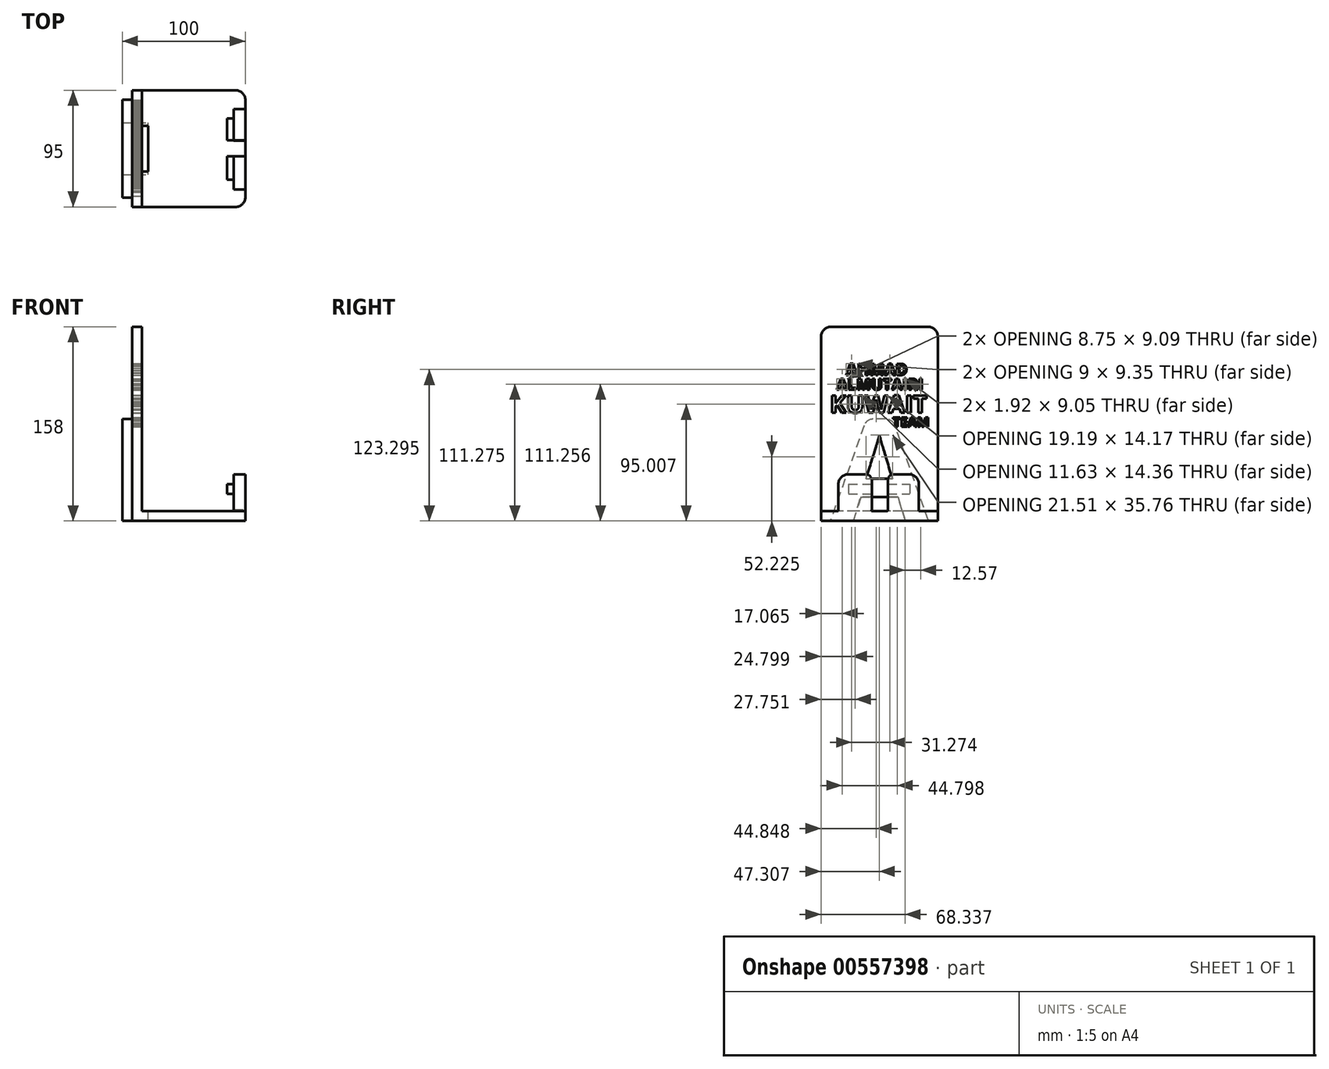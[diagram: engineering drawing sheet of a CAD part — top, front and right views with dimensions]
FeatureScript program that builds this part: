
annotation { "Feature Type Name" : "Feature", "Feature Type Description" : "" }
export const myFeature = defineFeature(function(context is Context, id is Id, definition is map)
    precondition{}
    {
        {
            var Q0;
            Q0=qCreatedBy(makeId("Top.planeOp"),FACE);
            var sketch = newSketch(context, id + "F0", { "sketchPlane" : qUnion([Q0])});
            skLineSegment(sketch, "E0.bottom", {"start": v(-46, -47.5) * mm, "end": v(46, -47.5) * mm});
            skLineSegment(sketch, "E0.top", {"start": v(-46, 47.5) * mm, "end": v(46, 47.5) * mm});
            skLineSegment(sketch, "E0.left", {"start": v(-46, -47.5) * mm, "end": v(-46, 47.5) * mm});
            skLineSegment(sketch, "E0.right", {"start": v(46, -47.5) * mm, "end": v(46, 47.5) * mm});
            skPoint(sketch, "E0.middle", {"position": v(0, 0) * mm});
            skSolve(sketch);
        }
        {
            var Q0;
            Q0=makeQuery(id+"F0.imprint","IMPRINT",FACE,{"disambiguationData":[TD([[makeQuery(id+"F0.imprint","IMPRINT",EDGE,{"derivedFrom":sQuery(id+"F0.wireOp",EDGE,"E0.bottom")}),1.0]])]});
            extrude(context, id + "F1", {"entities" : qUnion([Q0]), "depth" : 8 * mm, "offsetDistance" : 25 * mm});
        }
        {
            var Q0;
            Q0=makeQuery(id+"F1.opExtrude","CAP_FACE",FACE,{"disambiguationData":[OSD([sQuery(id+"F0.wireOp",EDGE,"E0.bottom"),sQuery(id+"F0.wireOp",EDGE,"E0.top"),sQuery(id+"F0.wireOp",EDGE,"E0.left"),sQuery(id+"F0.wireOp",EDGE,"E0.right")])],"isStart":false});
            var sketch = newSketch(context, id + "F2", { "sketchPlane" : qUnion([Q0])});
            skLineSegment(sketch, "E1.bottom", {"start": v(-46, 47.5) * mm, "end": v(-38, 47.5) * mm});
            skLineSegment(sketch, "E1.top", {"start": v(-46, -47.5) * mm, "end": v(-38, -47.5) * mm});
            skLineSegment(sketch, "E1.left", {"start": v(-46, 47.5) * mm, "end": v(-46, -47.5) * mm});
            skLineSegment(sketch, "E1.right", {"start": v(-38, 47.5) * mm, "end": v(-38, -47.5) * mm});
            skSolve(sketch);
        }
        {
            var Q0;
            Q0=qSketchRegion(id+"F2",true);
            extrude(context, id + "F3", {"entities" : qUnion([Q0]), "operationType" : NewBodyOperationType.ADD, "depth" : 150 * mm, "offsetDistance" : 25 * mm});
        }
        {
            var Q0;
            Q0=makeQuery(id+"F1.opExtrude","CAP_FACE",FACE,{"disambiguationData":[OSD([sQuery(id+"F0.wireOp",EDGE,"E0.bottom"),sQuery(id+"F0.wireOp",EDGE,"E0.top"),sQuery(id+"F0.wireOp",EDGE,"E0.left"),sQuery(id+"F0.wireOp",EDGE,"E0.right")])],"isStart":false});
            var sketch = newSketch(context, id + "F4", { "sketchPlane" : qUnion([Q0])});
            skLineSegment(sketch, "E2.bottom", {"start": v(46, 32.06) * mm, "end": v(36.5, 32.06) * mm});
            skLineSegment(sketch, "E2.top", {"start": v(46, -33.37) * mm, "end": v(36.5, -33.37) * mm});
            skLineSegment(sketch, "E2.left", {"start": v(46, 32.06) * mm, "end": v(46, -33.37) * mm});
            skLineSegment(sketch, "E2.right", {"start": v(36.5, 32.06) * mm, "end": v(36.5, -33.37) * mm});
            skSolve(sketch);
        }
        {
            var Q0;
            Q0=makeQuery(id+"F4.imprint","IMPRINT",FACE,{"disambiguationData":[TD([[makeQuery(id+"F4.imprint","IMPRINT",EDGE,{"derivedFrom":sQuery(id+"F4.wireOp",EDGE,"E2.bottom")}),1.0]])]});
            extrude(context, id + "F5", {"entities" : qUnion([Q0]), "operationType" : NewBodyOperationType.ADD, "depth" : 30 * mm, "offsetDistance" : 25 * mm});
        }
        {
            var Q0;
            Q0=makeQuery(id+"F3.boolean.opBoolean","MERGE",FACE,{"derivedFrom":[makeQuery(id+"F1.opExtrude","SWEPT_FACE",FACE,{"disambiguationData":[OSD([sQuery(id+"F0.wireOp",EDGE,"E0.left")])]}),makeQuery(id+"F3.opExtrude","SWEPT_FACE",FACE,{"disambiguationData":[OSD([sQuery(id+"F2.wireOp",EDGE,"E1.left")])]})]});
            var sketch = newSketch(context, id + "F6", { "sketchPlane" : qUnion([Q0])});
            skText(sketch, "E3", { "text": "A", "fontName": "OpenSans-Bold.ttf"});
            const initialGuessF6  = {"E3": [-0.03983, 0, 1, 0, 0.0833]};
            skSetInitialGuess(sketch, initialGuessF6);
            skSolve(sketch);
        }
        {
            var Q0;
            Q0=qSketchRegion(id+"F6",true);
            extrude(context, id + "F7", {"entities" : qUnion([Q0]), "operationType" : NewBodyOperationType.ADD, "depth" : 8 * mm, "offsetDistance" : 25 * mm});
        }
        {
            var Q0;
            Q0=makeQuery(id+"F7.boolean.opBoolean","SPLIT",FACE,{"disambiguationData":[TD([makeQuery(id+"F7.opExtrude","SWEPT_FACE",FACE,{"disambiguationData":[OSD([sQuery(id+"F6.wireOp",EDGE,"E3.sketch_text.stroke-8")])]})])],"derivedFrom":makeQuery(id+"F3.boolean.opBoolean","MERGE",FACE,{"derivedFrom":[makeQuery(id+"F1.opExtrude","SWEPT_FACE",FACE,{"disambiguationData":[OSD([sQuery(id+"F0.wireOp",EDGE,"E0.left")])]}),makeQuery(id+"F3.opExtrude","SWEPT_FACE",FACE,{"disambiguationData":[OSD([sQuery(id+"F2.wireOp",EDGE,"E1.left")])]})]})});
            var Q1;
            {var subQ0=sQuery(id+"F0.wireOp",EDGE,"E0.left");Q1=makeQuery(id+"F7.boolean.opBoolean","SPLIT",FACE,{"disambiguationData":[TD([makeQuery(id+"F7.opExtrude","SWEPT_FACE",FACE,{"disambiguationData":[OSD([sQuery(id+"F6.wireOp",EDGE,"E3.sketch_text.stroke-0")])]})])],"derivedFrom":makeQuery(id+"F3.boolean.opBoolean","MERGE",FACE,{"derivedFrom":[makeQuery(id+"F1.opExtrude","SWEPT_FACE",FACE,{"disambiguationData":[OSD([subQ0])]}),makeQuery(id+"F3.opExtrude","SWEPT_FACE",FACE,{"disambiguationData":[OSD([sQuery(id+"F2.wireOp",EDGE,"E1.left")])]})]})});}
            extrude(context, id + "F8", {"entities" : qUnion([Q0, Q1]), "operationType" : NewBodyOperationType.REMOVE, "oppositeDirection" : true, "depth" : 13 * mm, "offsetDistance" : 25 * mm});
        }
        {
            var Q0;
            Q0=makeQuery(id+"F1.opExtrude","CAP_FACE",FACE,{"disambiguationData":[OSD([sQuery(id+"F0.wireOp",EDGE,"E0.bottom"),sQuery(id+"F0.wireOp",EDGE,"E0.top"),sQuery(id+"F0.wireOp",EDGE,"E0.left"),sQuery(id+"F0.wireOp",EDGE,"E0.right")])],"isStart":false});
            var sketch = newSketch(context, id + "F9", { "sketchPlane" : qUnion([Q0])});
            skLineSegment(sketch, "E4.bottom", {"start": v(-46.36, -6.41) * mm, "end": v(46.36, -6.41) * mm});
            skLineSegment(sketch, "E4.top", {"start": v(-46.36, 6.41) * mm, "end": v(46.36, 6.41) * mm});
            skLineSegment(sketch, "E4.left", {"start": v(-46.36, -6.41) * mm, "end": v(-46.36, 6.41) * mm});
            skLineSegment(sketch, "E4.right", {"start": v(46.36, -6.41) * mm, "end": v(46.36, 6.41) * mm});
            skPoint(sketch, "E4.middle", {"position": v(0, 0) * mm});
            skSolve(sketch);
        }
        {
            var Q0;
            Q0=qSketchRegion(id+"F9",true);
            extrude(context, id + "F10", {"entities" : qUnion([Q0]), "operationType" : NewBodyOperationType.REMOVE, "depth" : 8 * mm, "offsetDistance" : 25 * mm});
        }
        {
            var Q0;
            Q0=makeQuery(id+"F5.opExtrude","CAP_EDGE",EDGE,{"disambiguationData":[OSD([sQuery(id+"F4.wireOp",EDGE,"E2.top")])],"isStart":false});
            var Q1;
            Q1=makeQuery(id+"F10.boolean.opBoolean","COPY",EDGE,{"derivedFrom":makeQuery(id+"F10.opExtrude","CAP_EDGE",EDGE,{"disambiguationData":[OSD([sQuery(id+"F9.wireOp",EDGE,"E4.bottom")])],"isStart":false})});
            var Q2;
            Q2=makeQuery(id+"F5.opExtrude","CAP_EDGE",EDGE,{"disambiguationData":[OSD([sQuery(id+"F4.wireOp",EDGE,"E2.bottom")])],"isStart":false});
            var Q3;
            Q3=makeQuery(id+"F10.boolean.opBoolean","COPY",EDGE,{"derivedFrom":makeQuery(id+"F10.opExtrude","CAP_EDGE",EDGE,{"disambiguationData":[OSD([sQuery(id+"F9.wireOp",EDGE,"E4.top")])],"isStart":false})});
            var Q4;
            Q4=makeQuery(id+"F1.opExtrude","SWEPT_EDGE",EDGE,{"disambiguationData":[OSD([sQuery(id+"F0.wireOp",EDGE,"E0.bottom"),sQuery(id+"F0.wireOp",EDGE,"E0.right")])]});
            var Q5;
            Q5=makeQuery(id+"F1.opExtrude","SWEPT_EDGE",EDGE,{"disambiguationData":[OSD([sQuery(id+"F0.wireOp",EDGE,"E0.top"),sQuery(id+"F0.wireOp",EDGE,"E0.right")])]});
            var Q6;
            Q6=makeQuery(id+"F3.opExtrude","CAP_EDGE",EDGE,{"disambiguationData":[OSD([sQuery(id+"F2.wireOp",EDGE,"E1.bottom")])],"isStart":false});
            var Q7;
            Q7=makeQuery(id+"F3.opExtrude","CAP_EDGE",EDGE,{"disambiguationData":[OSD([sQuery(id+"F2.wireOp",EDGE,"E1.top")])],"isStart":false});
            var Q8;
            Q8=makeQuery(id+"F7.opExtrude","SWEPT_EDGE",EDGE,{"disambiguationData":[OSD([sQuery(id+"F6.wireOp",EDGE,"E3.sketch_text.stroke-5"),sQuery(id+"F6.wireOp",EDGE,"E3.sketch_text.stroke-6")])]});
            var Q9;
            Q9=makeQuery(id+"F7.opExtrude","SWEPT_EDGE",EDGE,{"disambiguationData":[OSD([sQuery(id+"F6.wireOp",EDGE,"E3.sketch_text.stroke-4"),sQuery(id+"F6.wireOp",EDGE,"E3.sketch_text.stroke-5")])]});
            fillet(context, id + "F11", {"entities" : qUnion([Q0, Q1, Q2, Q3, Q4, Q5, Q6, Q7, Q8, Q9]), "radius" : 8 * mm, "tangentPropagation" : true, "allowEdgeOverflow" : false});
        }
        {
            var Q0;
            Q0=makeQuery(id+"F3.opExtrude","SWEPT_FACE",FACE,{"disambiguationData":[OSD([sQuery(id+"F2.wireOp",EDGE,"E1.right")])]});
            var sketch = newSketch(context, id + "F12", { "sketchPlane" : qUnion([Q0])});
            skSolve(sketch);
        }
        {
            var Q0;
            Q0=makeQuery(id+"F5.boolean.opBoolean","MERGE",FACE,{"derivedFrom":[makeQuery(id+"F1.opExtrude","SWEPT_FACE",FACE,{"disambiguationData":[OSD([sQuery(id+"F0.wireOp",EDGE,"E0.right")])]}),makeQuery(id+"F5.opExtrude","SWEPT_FACE",FACE,{"disambiguationData":[OSD([sQuery(id+"F4.wireOp",EDGE,"E2.left")])]})]});
            var sketch = newSketch(context, id + "F13", { "sketchPlane" : qUnion([Q0])});
            skLineSegment(sketch, "E5.bottom", {"start": v(-25.37, 30) * mm, "end": v(24.63, 30) * mm});
            skLineSegment(sketch, "E5.top", {"start": v(-25.37, 22) * mm, "end": v(24.63, 22) * mm});
            skLineSegment(sketch, "E5.left", {"start": v(-25.37, 30) * mm, "end": v(-25.37, 22) * mm});
            skLineSegment(sketch, "E5.right", {"start": v(24.63, 30) * mm, "end": v(24.63, 22) * mm});
            skSolve(sketch);
        }
        {
            var Q0;
            Q0=qSketchRegion(id+"F13",true);
            extrude(context, id + "F14", {"entities" : qUnion([Q0]), "operationType" : NewBodyOperationType.ADD, "oppositeDirection" : true, "depth" : 15 * mm, "offsetDistance" : 25 * mm});
        }
        {
            var Q0;
            Q0=qCreatedBy(makeId("Right.planeOp"),FACE);
            var sketch = newSketch(context, id + "F15", { "sketchPlane" : qUnion([Q0])});
            skLineSegment(sketch, "E6.bottom", {"start": v(-6.29, 8.45) * mm, "end": v(6.71, 8.45) * mm});
            skLineSegment(sketch, "E6.top", {"start": v(-6.29, 38.45) * mm, "end": v(6.71, 38.45) * mm});
            skLineSegment(sketch, "E6.left", {"start": v(-6.29, 8.45) * mm, "end": v(-6.29, 38.45) * mm});
            skLineSegment(sketch, "E6.right", {"start": v(6.71, 8.45) * mm, "end": v(6.71, 38.45) * mm});
            skSolve(sketch);
        }
        {
            var Q0;
            Q0=qSketchRegion(id+"F15",true);
            extrude(context, id + "F16", {"entities" : qUnion([Q0]), "operationType" : NewBodyOperationType.REMOVE, "depth" : 51 * mm, "offsetDistance" : 25 * mm});
        }
        {
            var Q0;
            Q0=makeQuery(id+"F16.boolean.opBoolean","INTERSECT",EDGE,{"derivedFrom":[makeQuery(id+"F5.opExtrude","CAP_FACE",FACE,{"disambiguationData":[OSD([sQuery(id+"F4.wireOp",EDGE,"E2.bottom"),sQuery(id+"F4.wireOp",EDGE,"E2.top"),sQuery(id+"F4.wireOp",EDGE,"E2.left"),sQuery(id+"F4.wireOp",EDGE,"E2.right")])],"isStart":false}),makeQuery(id+"F16.opExtrude","SWEPT_FACE",FACE,{"disambiguationData":[OSD([sQuery(id+"F15.wireOp",EDGE,"E6.left")])]})]});
            var Q1;
            Q1=makeQuery(id+"F16.boolean.opBoolean","INTERSECT",EDGE,{"derivedFrom":[makeQuery(id+"F5.opExtrude","CAP_FACE",FACE,{"disambiguationData":[OSD([sQuery(id+"F4.wireOp",EDGE,"E2.bottom"),sQuery(id+"F4.wireOp",EDGE,"E2.top"),sQuery(id+"F4.wireOp",EDGE,"E2.left"),sQuery(id+"F4.wireOp",EDGE,"E2.right")])],"isStart":false}),makeQuery(id+"F16.opExtrude","SWEPT_FACE",FACE,{"disambiguationData":[OSD([sQuery(id+"F15.wireOp",EDGE,"E6.right")])]})]});
            fillet(context, id + "F17", {"entities" : qUnion([Q0, Q1]), "radius" : 5 * mm, "tangentPropagation" : true, "allowEdgeOverflow" : false});
        }
        {
            var Q0;
            {var subQ0=sQuery(id+"F2.wireOp",EDGE,"E1.right");Q0=makeQuery(id+"F12.imprint","IMPRINT",FACE,{"disambiguationData":[TD([[makeQuery(id+"F12.imprint","IMPRINT",EDGE,{"derivedFrom":makeQuery(id+"F3.opExtrude","CAP_EDGE",EDGE,{"disambiguationData":[OSD([subQ0])],"isStart":false})}),1.0]])]});}
            var sketch = newSketch(context, id + "F18", { "sketchPlane" : qUnion([Q0])});
            skText(sketch, "E7", { "text": "KUWAIT", "fontName": "OpenSans-Bold.ttf"});
            const initialGuessF18  = {"E7": [-0.04043, 0.08802, 1, 0, 0.01429]};
            skSetInitialGuess(sketch, initialGuessF18);
            skSolve(sketch);
        }
        {
            var Q0;
            {var subQ0=sQuery(id+"F2.wireOp",EDGE,"E1.right");Q0=makeQuery(id+"F12.imprint","IMPRINT",FACE,{"disambiguationData":[TD([[makeQuery(id+"F12.imprint","IMPRINT",EDGE,{"derivedFrom":makeQuery(id+"F3.opExtrude","CAP_EDGE",EDGE,{"disambiguationData":[OSD([subQ0])],"isStart":false})}),1.0]])]});}
            var sketch = newSketch(context, id + "F19", { "sketchPlane" : qUnion([Q0])});
            skText(sketch, "E8", { "text": "TEAM", "fontName": "OpenSans-Bold.ttf"});
            const initialGuessF19  = {"E8": [0.01073, 0.07663, 1, 0, 0.00774]};
            skSetInitialGuess(sketch, initialGuessF19);
            skSolve(sketch);
        }
        {
            var Q0;
            {var subQ0=sQuery(id+"F2.wireOp",EDGE,"E1.right");Q0=makeQuery(id+"F12.imprint","IMPRINT",FACE,{"disambiguationData":[TD([[makeQuery(id+"F12.imprint","IMPRINT",EDGE,{"derivedFrom":makeQuery(id+"F3.opExtrude","CAP_EDGE",EDGE,{"disambiguationData":[OSD([subQ0])],"isStart":false})}),1.0]])]});}
            var sketch = newSketch(context, id + "F20", { "sketchPlane" : qUnion([Q0])});
            skText(sketch, "E9", { "text": "AHMAD\n", "fontName": "OpenSans-Bold.ttf"});
            const initialGuessF20  = {"E9": [-0.0272, 0.11862, 1, 0, 0.00939]};
            skSetInitialGuess(sketch, initialGuessF20);
            skSolve(sketch);
        }
        {
            var Q0;
            {var subQ0=sQuery(id+"F2.wireOp",EDGE,"E1.right");Q0=makeQuery(id+"F12.imprint","IMPRINT",FACE,{"disambiguationData":[TD([[makeQuery(id+"F12.imprint","IMPRINT",EDGE,{"derivedFrom":makeQuery(id+"F3.opExtrude","CAP_EDGE",EDGE,{"disambiguationData":[OSD([subQ0])],"isStart":false})}),1.0]])]});}
            var sketch = newSketch(context, id + "F21", { "sketchPlane" : qUnion([Q0])});
            skText(sketch, "E10", { "text": "ALMUTAIRI", "fontName": "OpenSans-Bold.ttf"});
            const initialGuessF21  = {"E10": [-0.03481, 0.10673, 1, 0, 0.00913]};
            skSetInitialGuess(sketch, initialGuessF21);
            skSolve(sketch);
        }
        {
            var Q0;
            Q0=qSketchRegion(id+"F21",true);
            var Q1;
            Q1=qSketchRegion(id+"F18",true);
            var Q2;
            Q2=qSketchRegion(id+"F19",true);
            var Q3;
            Q3=qSketchRegion(id+"F20",true);
            extrude(context, id + "F22", {"entities" : qUnion([Q0, Q1, Q2, Q3]), "operationType" : NewBodyOperationType.REMOVE, "oppositeDirection" : true, "depth" : 25 * mm, "offsetDistance" : 25 * mm});
        }
    });
